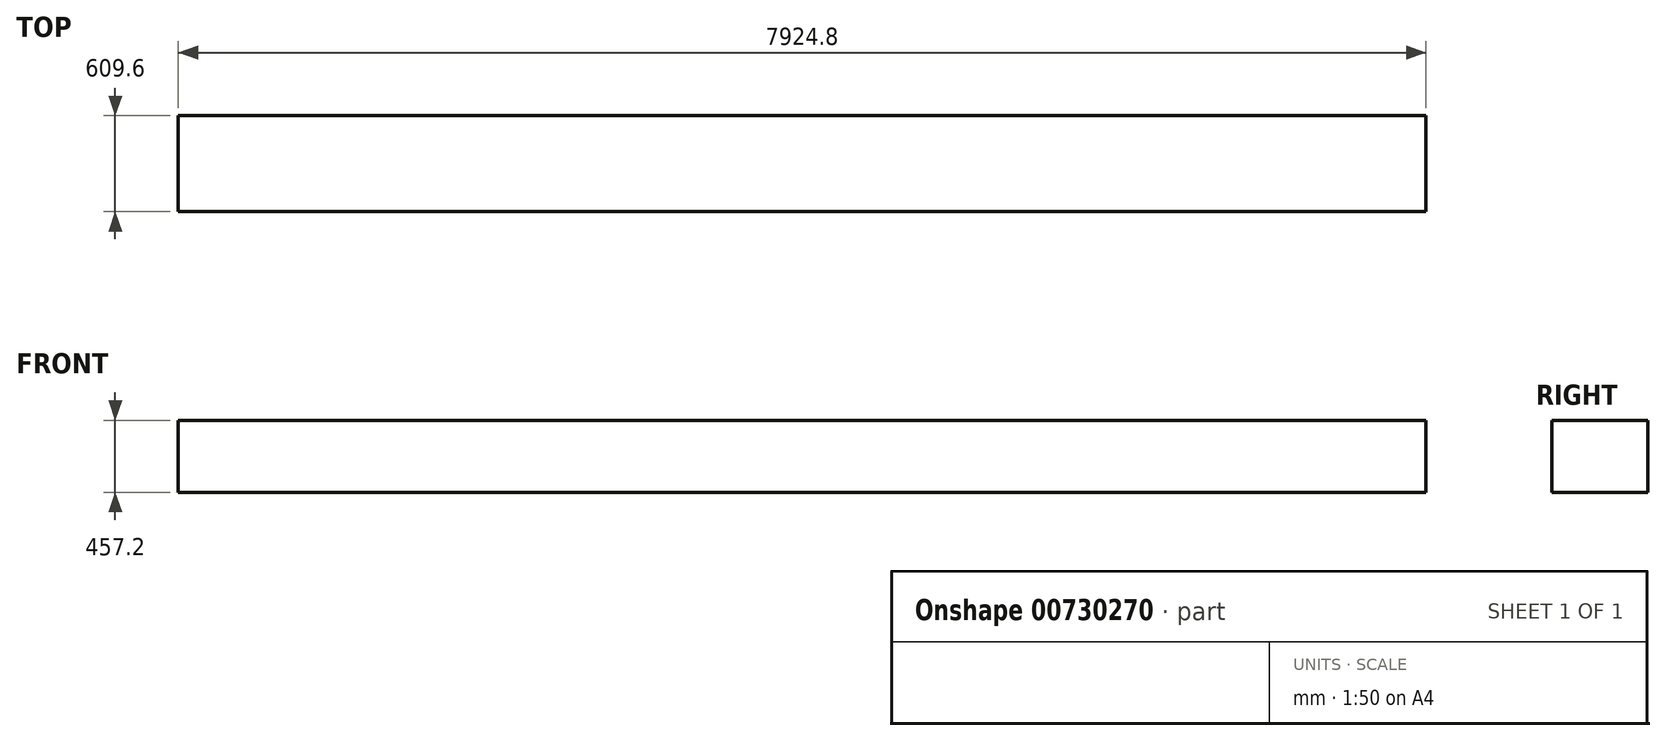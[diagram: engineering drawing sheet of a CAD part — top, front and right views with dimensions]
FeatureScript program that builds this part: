
annotation { "Feature Type Name" : "Feature", "Feature Type Description" : "" }
export const myFeature = defineFeature(function(context is Context, id is Id, definition is map)
    precondition{}
    {
        {
            var Q0;
            Q0=qCreatedBy(makeId("Right.planeOp"),FACE);
            var sketch = newSketch(context, id + "F0", { "sketchPlane" : qUnion([Q0])});
            skLineSegment(sketch, "E0.bottom", {"start": v(304.8, 228.6) * mm, "end": v(-304.8, 228.6) * mm});
            skLineSegment(sketch, "E0.top", {"start": v(304.8, -228.6) * mm, "end": v(-304.8, -228.6) * mm});
            skLineSegment(sketch, "E0.left", {"start": v(304.8, 228.6) * mm, "end": v(304.8, -228.6) * mm});
            skLineSegment(sketch, "E0.right", {"start": v(-304.8, 228.6) * mm, "end": v(-304.8, -228.6) * mm});
            skPoint(sketch, "E0.middle", {"position": v(0, 0) * mm});
            skSolve(sketch);
        }
        {
            var Q0;
            Q0=qSketchRegion(id+"F0",true);
            extrude(context, id + "F1", {"entities" : qUnion([Q0]), "endBound" : BoundingType.SYMMETRIC, "depth" : 7924.8 * mm});
        }
        {
            var Q0;
            Q0=qCreatedBy(makeId("Front.planeOp"),FACE);
            var sketch = newSketch(context, id + "F2", { "sketchPlane" : qUnion([Q0])});
            skLineSegment(sketch, "E1", {"start": v(-3962.4, 0) * mm, "end": v(2651.36, -2944.64) * mm, "construction": true});
            skLineSegment(sketch, "E2", {"start": v(2651.36, -2944.64) * mm, "end": v(3962.4, 0) * mm, "construction": true});
            skLineSegment(sketch, "E3", {"start": v(3962.4, 0) * mm, "end": v(-3962.4, 0) * mm, "construction": true});
            skSolve(sketch);
        }
    });
